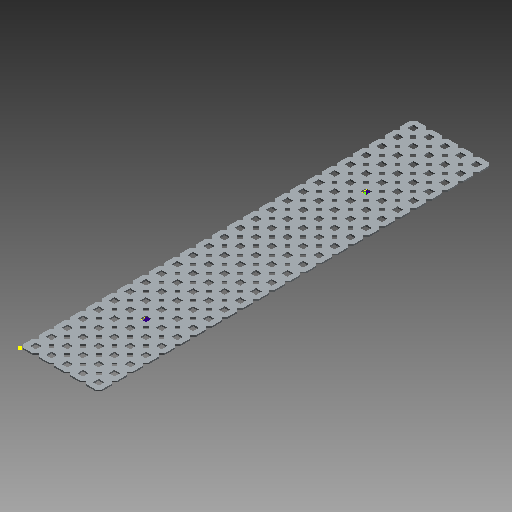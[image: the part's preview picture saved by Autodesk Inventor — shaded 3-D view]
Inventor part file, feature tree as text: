
AUTODESK INVENTOR PART (.ipt)
format: ipt  version: 2018 (Build 220112000, 112)  size: 2,280,960 bytes
history: native  units: mm (DEFAULTED — no unit token found)
features: other x125, extrude x125, sketch x3, imported_body x1, pattern_linear x1
ambient origin geometry x8: Origin, YZ Plane, XZ Plane, XY Plane, X Axis, Y Axis, Z Axis, Center Point
bodies: Solid1 (feature_tree)
feature tree (255):
  imported_body  "Base1"
  pattern_linear  "Rectangular Pattern1"  Count1=25  [1 undecoded]
  sketch  "Sketch2"  dims[d2=0.0mm d3=250.0mm]
  sketch  "Sketch3"  dims[d5=12.7mm d6=50.0mm d8=12.7mm d9=0.0mm d10=0.0mm d11=0.0mm d12=0.0mm d13=0.0mm d14=0.0mm d15=0.0mm d16=0.0mm d17=0.0mm d18=0.0mm d19=0.0mm d20=0.0mm d21=0.0mm d22=0.0mm d23=0.0mm d24=0.0mm d25=0.0mm d26=0.0mm d27=0.0mm d28=0.0mm d29=0.0mm d30=0.0mm d31=0.0mm d32=0.0mm d33=0.0mm d34=0.0mm d35=0.0mm d36=0.0mm d37=0.0mm d38=0.0mm d39=0.0mm d40=0.0mm d41=0.0mm d42=0.0mm d43=0.0mm d44=0.0mm d45=0.0mm d46=0.0mm d47=0.0mm d48=0.0mm d49=0.0mm d50=0.0mm d51=0.0mm d52=0.0mm d53=0.0mm d54=0.0mm d55=0.0mm d56=0.0mm d57=0.0mm d58=0.0mm d59=0.0mm d60=0.0mm d61=0.0mm d62=0.0mm d63=0.0mm d64=0.0mm d65=0.0mm d66=0.0mm d67=0.0mm d68=0.0mm d69=0.0mm d70=0.0mm d71=0.0mm d72=0.0mm d73=0.0mm d74=0.0mm d75=0.0mm d76=0.0mm d77=0.0mm d78=0.0mm d79=0.0mm d80=0.0mm d81=0.0mm d82=0.0mm d83=0.0mm d84=0.0mm d85=0.0mm d86=0.0mm d87=0.0mm d88=0.0mm d89=0.0mm d90=0.0mm d91=0.0mm d92=0.0mm d93=0.0mm d94=0.0mm d95=0.0mm d96=0.0mm d97=0.0mm d98=0.0mm d99=0.0mm d100=0.0mm d101=0.0mm d102=0.0mm d103=0.0mm d104=0.0mm d105=0.0mm d106=0.0mm d107=0.0mm d108=0.0mm d109=0.0mm d110=0.0mm d111=0.0mm d112=0.0mm d113=0.0mm d114=0.0mm d115=0.0mm d116=0.0mm d117=0.0mm d118=0.0mm d119=0.0mm d120=0.0mm d121=0.0mm d122=0.0mm d123=0.0mm d124=0.0mm d125=0.0mm d126=0.0mm d127=0.0mm d128=0.0mm d129=0.0mm d130=0.0mm d131=0.0mm d132=0.0mm d133=0.0mm d134=0.0mm d135=0.0mm d136=0.0mm d137=0.0mm d138=0.0mm d139=0.0mm d140=0.0mm d141=0.0mm d142=0.0mm d143=0.0mm d144=0.0mm d145=0.0mm d146=0.0mm d147=0.0mm d148=0.0mm d149=0.0mm d150=0.0mm d151=0.0mm d152=0.0mm d153=0.0mm d154=0.0mm d155=0.0mm d156=0.0mm d157=0.0mm d158=0.0mm d159=0.0mm d160=0.0mm d161=0.0mm d162=0.0mm d163=0.0mm d164=0.0mm d165=0.0mm d166=0.0mm d167=0.0mm d168=0.0mm d169=0.0mm d170=0.0mm d171=0.0mm d172=0.0mm d173=0.0mm d174=0.0mm d175=0.0mm d176=0.0mm d177=0.0mm d178=0.0mm d179=0.0mm d180=0.0mm d181=0.0mm d182=0.0mm d183=0.0mm d184=0.0mm d185=0.0mm d186=0.0mm d187=0.0mm d188=0.0mm d189=0.0mm d190=0.0mm d191=0.0mm d192=0.0mm d193=0.0mm d194=0.0mm d195=0.0mm d196=0.0mm d197=0.0mm d198=0.0mm d199=0.0mm d200=0.0mm d201=0.0mm d202=0.0mm d203=0.0mm d204=0.0mm d205=0.0mm d206=0.0mm d207=0.0mm d208=0.0mm d209=0.0mm d210=0.0mm d211=0.0mm d212=0.0mm d213=0.0mm d214=0.0mm d215=0.0mm d216=0.0mm d217=0.0mm d218=0.0mm d219=0.0mm d220=0.0mm d221=0.0mm d222=0.0mm d223=0.0mm d224=0.0mm d225=0.0mm d226=0.0mm d227=0.0mm d228=0.0mm d229=0.0mm d230=0.0mm d231=0.0mm d232=0.0mm d233=0.0mm d234=0.0mm d235=0.0mm d236=0.0mm d237=0.0mm d238=0.0mm d239=0.0mm d240=0.0mm d241=0.0mm d242=0.0mm d243=0.0mm d244=0.0mm d245=0.0mm d246=0.0mm d247=0.0mm d248=0.0mm d249=0.0mm d250=0.0mm d251=0.0mm d252=0.0mm d253=0.0mm d254=0.0mm d255=0.0mm d256=0.0mm d257=0.0mm d258=0.0mm]
  sketch  "Sketch1"  dims[d1=1.1684mm]
  other  "Srf1"
  other  "Srf2"
  other  "Srf3"
  other  "Srf4"
  other  "Srf5"
  other  "Srf6"
  other  "Srf7"
  other  "Srf8"
  other  "Srf9"
  other  "Srf10"
  other  "Srf11"
  other  "Srf12"
  other  "Srf13"
  other  "Srf14"
  other  "Srf15"
  other  "Srf16"
  other  "Srf17"
  other  "Srf18"
  other  "Srf19"
  other  "Srf20"
  other  "Srf21"
  other  "Srf22"
  other  "Srf23"
  other  "Srf24"
  other  "Srf25"
  other  "Srf26"
  other  "Srf27"
  other  "Srf28"
  other  "Srf29"
  other  "Srf30"
  other  "Srf31"
  other  "Srf32"
  other  "Srf33"
  other  "Srf34"
  other  "Srf35"
  other  "Srf36"
  other  "Srf37"
  other  "Srf38"
  other  "Srf39"
  other  "Srf40"
  other  "Srf41"
  other  "Srf42"
  other  "Srf43"
  other  "Srf44"
  other  "Srf45"
  other  "Srf46"
  other  "Srf47"
  other  "Srf48"
  other  "Srf49"
  other  "Srf50"
  other  "Srf51"
  other  "Srf52"
  other  "Srf53"
  other  "Srf54"
  other  "Srf55"
  other  "Srf56"
  other  "Srf57"
  other  "Srf58"
  other  "Srf59"
  other  "Srf60"
  other  "Srf61"
  other  "Srf62"
  other  "Srf63"
  other  "Srf64"
  other  "Srf65"
  other  "Srf66"
  other  "Srf67"
  other  "Srf68"
  other  "Srf69"
  other  "Srf70"
  other  "Srf71"
  other  "Srf72"
  other  "Srf73"
  other  "Srf74"
  other  "Srf75"
  other  "Srf76"
  other  "Srf77"
  other  "Srf78"
  other  "Srf79"
  other  "Srf80"
  other  "Srf81"
  other  "Srf82"
  other  "Srf83"
  other  "Srf84"
  other  "Srf85"
  other  "Srf86"
  other  "Srf87"
  other  "Srf88"
  other  "Srf89"
  other  "Srf90"
  other  "Srf91"
  other  "Srf92"
  other  "Srf93"
  other  "Srf94"
  other  "Srf95"
  other  "Srf96"
  other  "Srf97"
  other  "Srf98"
  other  "Srf99"
  other  "Srf100"
  other  "Srf101"
  other  "Srf102"
  other  "Srf103"
  other  "Srf104"
  other  "Srf105"
  other  "Srf106"
  other  "Srf107"
  other  "Srf108"
  other  "Srf109"
  other  "Srf110"
  other  "Srf111"
  other  "Srf112"
  other  "Srf113"
  other  "Srf114"
  other  "Srf115"
  other  "Srf116"
  other  "Srf117"
  other  "Srf118"
  other  "Srf119"
  other  "Srf120"
  other  "Srf121"
  other  "Srf122"
  other  "Srf123"
  other  "Srf124"
  other  "Srf125"
  extrude  "ExtrusionSrf1"  Depth=50.0mm
  extrude  "ExtrusionSrf2"  TaperAngle=0.0deg  [1 undecoded]
  extrude  "ExtrusionSrf3"  TaperAngle=0.0deg  [1 undecoded]
  extrude  "ExtrusionSrf4"  TaperAngle=0.0deg  [1 undecoded]
  extrude  "ExtrusionSrf5"  TaperAngle=0.0deg  [1 undecoded]
  extrude  "ExtrusionSrf6"  TaperAngle=0.0deg  [1 undecoded]
  extrude  "ExtrusionSrf7"  TaperAngle=0.0deg  [1 undecoded]
  extrude  "ExtrusionSrf8"  TaperAngle=0.0deg  [1 undecoded]
  extrude  "ExtrusionSrf9"  TaperAngle=0.0deg  [1 undecoded]
  extrude  "ExtrusionSrf10"  TaperAngle=0.0deg  [1 undecoded]
  extrude  "ExtrusionSrf11"  TaperAngle=0.0deg  [1 undecoded]
  extrude  "ExtrusionSrf12"  TaperAngle=0.0deg  [1 undecoded]
  extrude  "ExtrusionSrf13"  TaperAngle=0.0deg  [1 undecoded]
  extrude  "ExtrusionSrf14"  TaperAngle=0.0deg  [1 undecoded]
  extrude  "ExtrusionSrf15"  TaperAngle=0.0deg  [1 undecoded]
  extrude  "ExtrusionSrf16"  TaperAngle=0.0deg  [1 undecoded]
  extrude  "ExtrusionSrf17"  TaperAngle=0.0deg  [1 undecoded]
  extrude  "ExtrusionSrf18"  TaperAngle=0.0deg  [1 undecoded]
  extrude  "ExtrusionSrf19"  TaperAngle=0.0deg  [1 undecoded]
  extrude  "ExtrusionSrf20"  TaperAngle=0.0deg  [1 undecoded]
  extrude  "ExtrusionSrf21"  TaperAngle=0.0deg  [1 undecoded]
  extrude  "ExtrusionSrf22"  TaperAngle=0.0deg  [1 undecoded]
  extrude  "ExtrusionSrf23"  TaperAngle=0.0deg  [1 undecoded]
  extrude  "ExtrusionSrf24"  TaperAngle=0.0deg  [1 undecoded]
  extrude  "ExtrusionSrf25"  TaperAngle=0.0deg  [1 undecoded]
  extrude  "ExtrusionSrf26"  TaperAngle=0.0deg  [1 undecoded]
  extrude  "ExtrusionSrf27"  TaperAngle=0.0deg  [1 undecoded]
  extrude  "ExtrusionSrf28"  TaperAngle=0.0deg  [1 undecoded]
  extrude  "ExtrusionSrf29"  TaperAngle=0.0deg  [1 undecoded]
  extrude  "ExtrusionSrf30"  TaperAngle=0.0deg  [1 undecoded]
  extrude  "ExtrusionSrf31"  TaperAngle=0.0deg  [1 undecoded]
  extrude  "ExtrusionSrf32"  TaperAngle=0.0deg  [1 undecoded]
  extrude  "ExtrusionSrf33"  TaperAngle=0.0deg  [1 undecoded]
  extrude  "ExtrusionSrf34"  TaperAngle=0.0deg  [1 undecoded]
  extrude  "ExtrusionSrf35"  TaperAngle=0.0deg  [1 undecoded]
  extrude  "ExtrusionSrf36"  TaperAngle=0.0deg  [1 undecoded]
  extrude  "ExtrusionSrf37"  TaperAngle=0.0deg  [1 undecoded]
  extrude  "ExtrusionSrf38"  TaperAngle=0.0deg  [1 undecoded]
  extrude  "ExtrusionSrf39"  TaperAngle=0.0deg  [1 undecoded]
  extrude  "ExtrusionSrf40"  TaperAngle=0.0deg  [1 undecoded]
  extrude  "ExtrusionSrf41"  TaperAngle=0.0deg  [1 undecoded]
  extrude  "ExtrusionSrf42"  TaperAngle=0.0deg  [1 undecoded]
  extrude  "ExtrusionSrf43"  TaperAngle=0.0deg  [1 undecoded]
  extrude  "ExtrusionSrf44"  TaperAngle=0.0deg  [1 undecoded]
  extrude  "ExtrusionSrf45"  TaperAngle=0.0deg  [1 undecoded]
  extrude  "ExtrusionSrf46"  TaperAngle=0.0deg  [1 undecoded]
  extrude  "ExtrusionSrf47"  TaperAngle=0.0deg  [1 undecoded]
  extrude  "ExtrusionSrf48"  TaperAngle=0.0deg  [1 undecoded]
  extrude  "ExtrusionSrf49"  TaperAngle=0.0deg  [1 undecoded]
  extrude  "ExtrusionSrf50"  TaperAngle=0.0deg  [1 undecoded]
  extrude  "ExtrusionSrf51"  TaperAngle=0.0deg  [1 undecoded]
  extrude  "ExtrusionSrf52"  TaperAngle=0.0deg  [1 undecoded]
  extrude  "ExtrusionSrf53"  TaperAngle=0.0deg  [1 undecoded]
  extrude  "ExtrusionSrf54"  TaperAngle=0.0deg  [1 undecoded]
  extrude  "ExtrusionSrf55"  TaperAngle=0.0deg  [1 undecoded]
  extrude  "ExtrusionSrf56"  TaperAngle=0.0deg  [1 undecoded]
  extrude  "ExtrusionSrf57"  TaperAngle=0.0deg  [1 undecoded]
  extrude  "ExtrusionSrf58"  TaperAngle=0.0deg  [1 undecoded]
  extrude  "ExtrusionSrf59"  TaperAngle=0.0deg  [1 undecoded]
  extrude  "ExtrusionSrf60"  TaperAngle=0.0deg  [1 undecoded]
  extrude  "ExtrusionSrf61"  TaperAngle=0.0deg  [1 undecoded]
  extrude  "ExtrusionSrf62"  TaperAngle=0.0deg  [1 undecoded]
  extrude  "ExtrusionSrf63"  TaperAngle=0.0deg  [1 undecoded]
  extrude  "ExtrusionSrf64"  TaperAngle=0.0deg  [1 undecoded]
  extrude  "ExtrusionSrf65"  TaperAngle=0.0deg  [1 undecoded]
  extrude  "ExtrusionSrf66"  TaperAngle=0.0deg  [1 undecoded]
  extrude  "ExtrusionSrf67"  TaperAngle=0.0deg  [1 undecoded]
  extrude  "ExtrusionSrf68"  TaperAngle=0.0deg  [1 undecoded]
  extrude  "ExtrusionSrf69"  TaperAngle=0.0deg  [1 undecoded]
  extrude  "ExtrusionSrf70"  TaperAngle=0.0deg  [1 undecoded]
  extrude  "ExtrusionSrf71"  TaperAngle=0.0deg  [1 undecoded]
  extrude  "ExtrusionSrf72"  TaperAngle=0.0deg  [1 undecoded]
  extrude  "ExtrusionSrf73"  TaperAngle=0.0deg  [1 undecoded]
  extrude  "ExtrusionSrf74"  TaperAngle=0.0deg  [1 undecoded]
  extrude  "ExtrusionSrf75"  TaperAngle=0.0deg  [1 undecoded]
  extrude  "ExtrusionSrf76"  TaperAngle=0.0deg  [1 undecoded]
  extrude  "ExtrusionSrf77"  TaperAngle=0.0deg  [1 undecoded]
  extrude  "ExtrusionSrf78"  TaperAngle=0.0deg  [1 undecoded]
  extrude  "ExtrusionSrf79"  TaperAngle=0.0deg  [1 undecoded]
  extrude  "ExtrusionSrf80"  TaperAngle=0.0deg  [1 undecoded]
  extrude  "ExtrusionSrf81"  TaperAngle=0.0deg  [1 undecoded]
  extrude  "ExtrusionSrf82"  TaperAngle=0.0deg  [1 undecoded]
  extrude  "ExtrusionSrf83"  TaperAngle=0.0deg  [1 undecoded]
  extrude  "ExtrusionSrf84"  TaperAngle=0.0deg  [1 undecoded]
  extrude  "ExtrusionSrf85"  TaperAngle=0.0deg  [1 undecoded]
  extrude  "ExtrusionSrf86"  TaperAngle=0.0deg  [1 undecoded]
  extrude  "ExtrusionSrf87"  TaperAngle=0.0deg  [1 undecoded]
  extrude  "ExtrusionSrf88"  TaperAngle=0.0deg  [1 undecoded]
  extrude  "ExtrusionSrf89"  TaperAngle=0.0deg  [1 undecoded]
  extrude  "ExtrusionSrf90"  TaperAngle=0.0deg  [1 undecoded]
  extrude  "ExtrusionSrf91"  TaperAngle=0.0deg  [1 undecoded]
  extrude  "ExtrusionSrf92"  TaperAngle=0.0deg  [1 undecoded]
  extrude  "ExtrusionSrf93"  TaperAngle=0.0deg  [1 undecoded]
  extrude  "ExtrusionSrf94"  TaperAngle=0.0deg  [1 undecoded]
  extrude  "ExtrusionSrf95"  TaperAngle=0.0deg  [1 undecoded]
  extrude  "ExtrusionSrf96"  TaperAngle=0.0deg  [1 undecoded]
  extrude  "ExtrusionSrf97"  TaperAngle=0.0deg  [1 undecoded]
  extrude  "ExtrusionSrf98"  TaperAngle=0.0deg  [1 undecoded]
  extrude  "ExtrusionSrf99"  TaperAngle=0.0deg  [1 undecoded]
  extrude  "ExtrusionSrf100"  TaperAngle=0.0deg  [1 undecoded]
  extrude  "ExtrusionSrf101"  TaperAngle=0.0deg  [1 undecoded]
  extrude  "ExtrusionSrf102"  TaperAngle=0.0deg  [1 undecoded]
  extrude  "ExtrusionSrf103"  TaperAngle=0.0deg  [1 undecoded]
  extrude  "ExtrusionSrf104"  TaperAngle=0.0deg  [1 undecoded]
  extrude  "ExtrusionSrf105"  TaperAngle=0.0deg  [1 undecoded]
  extrude  "ExtrusionSrf106"  TaperAngle=0.0deg  [1 undecoded]
  extrude  "ExtrusionSrf107"  TaperAngle=0.0deg  [1 undecoded]
  extrude  "ExtrusionSrf108"  TaperAngle=0.0deg  [1 undecoded]
  extrude  "ExtrusionSrf109"  TaperAngle=0.0deg  [1 undecoded]
  extrude  "ExtrusionSrf110"  TaperAngle=0.0deg  [1 undecoded]
  extrude  "ExtrusionSrf111"  TaperAngle=0.0deg  [1 undecoded]
  extrude  "ExtrusionSrf112"  TaperAngle=0.0deg  [1 undecoded]
  extrude  "ExtrusionSrf113"  TaperAngle=0.0deg  [1 undecoded]
  extrude  "ExtrusionSrf114"  TaperAngle=0.0deg  [1 undecoded]
  extrude  "ExtrusionSrf115"  TaperAngle=0.0deg  [1 undecoded]
  extrude  "ExtrusionSrf116"  TaperAngle=0.0deg  [1 undecoded]
  extrude  "ExtrusionSrf117"  TaperAngle=0.0deg  [1 undecoded]
  extrude  "ExtrusionSrf118"  TaperAngle=0.0deg  [1 undecoded]
  extrude  "ExtrusionSrf119"  TaperAngle=0.0deg  [1 undecoded]
  extrude  "ExtrusionSrf120"  TaperAngle=0.0deg  [1 undecoded]
  extrude  "ExtrusionSrf121"  TaperAngle=0.0deg  [1 undecoded]
  extrude  "ExtrusionSrf122"  TaperAngle=0.0deg  [1 undecoded]
  extrude  "ExtrusionSrf123"  TaperAngle=0.0deg  [1 undecoded]
  extrude  "ExtrusionSrf124"  TaperAngle=0.0deg  [1 undecoded]
  extrude  "ExtrusionSrf125"  TaperAngle=0.0deg  [1 undecoded]
note: 125 required parameter values undecoded (feature->parameter linkage not recoverable at this tier; creation-order binding heuristic only, values carry confidence <= 0.55)
